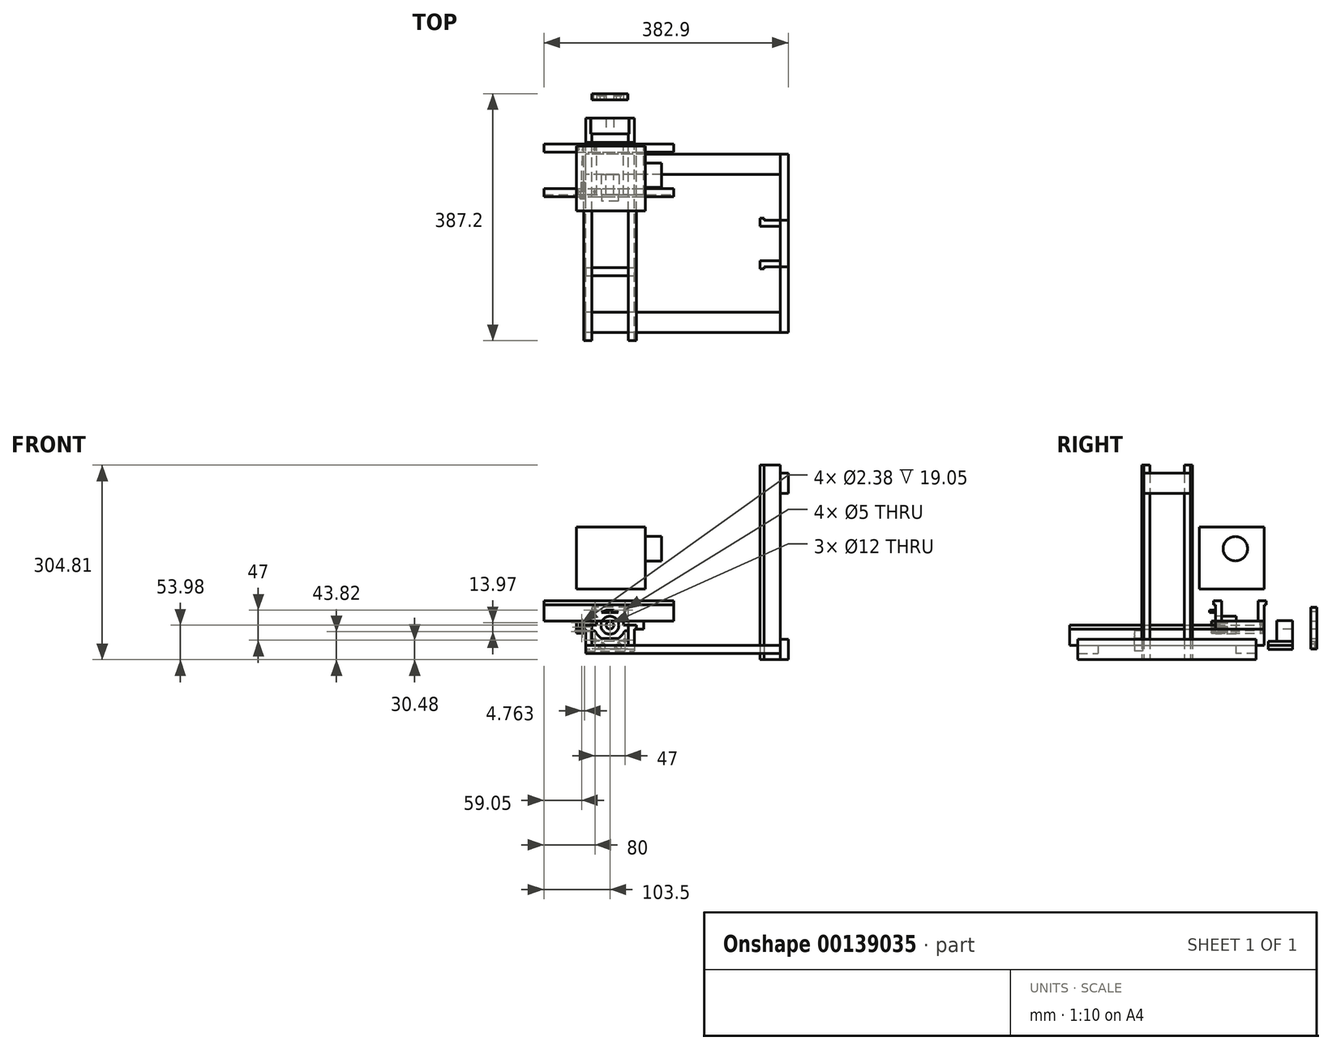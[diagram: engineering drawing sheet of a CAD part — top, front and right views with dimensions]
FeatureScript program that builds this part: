
annotation { "Feature Type Name" : "Feature", "Feature Type Description" : "" }
export const myFeature = defineFeature(function(context is Context, id is Id, definition is map)
    precondition{}
    {
        {
            var Q0;
            Q0=qCreatedBy(makeId("Front.planeOp"),FACE);
            var sketch = newSketch(context, id + "F0", { "sketchPlane" : qUnion([Q0])});
            skLineSegment(sketch, "E0.bottom", {"start": v(-38.1, 0) * mm, "end": v(-28.58, 0) * mm});
            skLineSegment(sketch, "E0.top", {"start": v(-41.27, 31.75) * mm, "end": v(-28.57, 31.75) * mm});
            skLineSegment(sketch, "E0.right", {"start": v(-28.58, 0) * mm, "end": v(-28.57, 31.75) * mm});
            skPoint(sketch, "E1", {"position": v(-41.27, 25.4) * mm});
            skLineSegment(sketch, "E2", {"start": v(-41.27, 31.75) * mm, "end": v(-41.27, 25.4) * mm});
            skLineSegment(sketch, "E3", {"start": v(-38.1, 25.4) * mm, "end": v(-38.1, 0) * mm});
            skLineSegment(sketch, "E4", {"start": v(-41.27, 25.4) * mm, "end": v(-38.1, 25.4) * mm});
            skPoint(sketch, "E5", {"position": v(-33.34, 0) * mm});
            skLineSegment(sketch, "E6.MirrorCS", {"start": v(28.58, 0) * mm, "end": v(28.57, 31.75) * mm});
            skLineSegment(sketch, "E7.MirrorCS", {"start": v(38.1, 0) * mm, "end": v(28.58, 0) * mm});
            skLineSegment(sketch, "E8.MirrorCS", {"start": v(38.1, 25.4) * mm, "end": v(38.1, 0) * mm});
            skLineSegment(sketch, "E9.MirrorCS", {"start": v(41.27, 25.4) * mm, "end": v(38.1, 25.4) * mm});
            skLineSegment(sketch, "E10.MirrorCS", {"start": v(41.27, 31.75) * mm, "end": v(41.27, 25.4) * mm});
            skLineSegment(sketch, "E11.MirrorCS", {"start": v(41.27, 31.75) * mm, "end": v(28.57, 31.75) * mm});
            skSolve(sketch);
        }
        {
            var Q0;
            Q0 = qSketchRegion(id + "F0", true);
            extrude(context, id + "F1", {"entities" : qUnion([Q0]), "depth" : 304.8 * mm});
        }
        {
            var Q0;
            Q0=makeQuery(id+"F1.opExtrude","CAP_FACE",FACE,{"disambiguationData":[OSD([sQuery(id+"F0.wireOp",EDGE,"E0.bottom"),sQuery(id+"F0.wireOp",EDGE,"E0.top"),sQuery(id+"F0.wireOp",EDGE,"E0.right"),sQuery(id+"F0.wireOp",EDGE,"E2"),sQuery(id+"F0.wireOp",EDGE,"E3"),sQuery(id+"F0.wireOp",EDGE,"E4")])],"isStart":true});
            var sketch = newSketch(context, id + "F2", { "sketchPlane" : qUnion([Q0])});
            skLineSegment(sketch, "E12", {"start": v(28.57, 31.75) * mm, "end": v(41.27, 31.75) * mm});
            skLineSegment(sketch, "E13", {"start": v(41.27, 31.75) * mm, "end": v(41.27, 25.4) * mm});
            skLineSegment(sketch, "E14", {"start": v(41.27, 25.4) * mm, "end": v(52.7, 25.4) * mm});
            skLineSegment(sketch, "E15", {"start": v(52.7, 25.4) * mm, "end": v(52.7, 38.1) * mm});
            skLineSegment(sketch, "E16", {"start": v(52.7, 38.1) * mm, "end": v(20.95, 38.1) * mm});
            skLineSegment(sketch, "E17", {"start": v(20.95, 38.1) * mm, "end": v(20.95, 31.75) * mm});
            skLineSegment(sketch, "E18", {"start": v(20.95, 31.75) * mm, "end": v(28.57, 31.75) * mm});
            skLineSegment(sketch, "E19.MirrorCS", {"start": v(-20.95, 38.1) * mm, "end": v(-20.95, 31.75) * mm});
            skLineSegment(sketch, "E20.MirrorCS", {"start": v(-20.95, 31.75) * mm, "end": v(-28.57, 31.75) * mm});
            skLineSegment(sketch, "E21.MirrorCS", {"start": v(-28.57, 31.75) * mm, "end": v(-41.27, 31.75) * mm});
            skLineSegment(sketch, "E22.MirrorCS", {"start": v(-41.27, 31.75) * mm, "end": v(-41.27, 25.4) * mm});
            skLineSegment(sketch, "E23.MirrorCS", {"start": v(-41.27, 25.4) * mm, "end": v(-52.7, 25.4) * mm});
            skLineSegment(sketch, "E24.MirrorCS", {"start": v(-52.7, 25.4) * mm, "end": v(-52.7, 38.1) * mm});
            skLineSegment(sketch, "E25.MirrorCS", {"start": v(-52.7, 38.1) * mm, "end": v(-20.95, 38.1) * mm});
            skSolve(sketch);
        }
        {
            var Q0;
            Q0=makeQuery(id+"F2.imprint","IMPRINT",FACE,{"disambiguationData":[TD([[makeQuery(id+"F2.imprint","IMPRINT",EDGE,{"derivedFrom":sQuery(id+"F2.wireOp",EDGE,"E12")}),-1.0]])]});
            var Q1;
            Q1=makeQuery(id+"F2.imprint","IMPRINT",FACE,{"disambiguationData":[TD([[makeQuery(id+"F2.imprint","IMPRINT",EDGE,{"derivedFrom":sQuery(id+"F2.wireOp",EDGE,"E19.MirrorCS")}),-1.0]])]});
            extrude(context, id + "F3", {"entities" : qUnion([Q0, Q1]), "oppositeDirection" : true, "depth" : 76.2 * mm});
        }
        {
            var Q0;
            Q0=makeQuery(id+"F1.opExtrude","CAP_FACE",FACE,{"disambiguationData":[OSD([sQuery(id+"F0.wireOp",EDGE,"E0.bottom"),sQuery(id+"F0.wireOp",EDGE,"E0.top"),sQuery(id+"F0.wireOp",EDGE,"E0.right"),sQuery(id+"F0.wireOp",EDGE,"E2"),sQuery(id+"F0.wireOp",EDGE,"E3"),sQuery(id+"F0.wireOp",EDGE,"E4")])],"isStart":true});
            var sketch = newSketch(context, id + "F4", { "sketchPlane" : qUnion([Q0])});
            skLineSegment(sketch, "E26.bottom", {"start": v(38.1, 25.4) * mm, "end": v(52.7, 25.4) * mm});
            skLineSegment(sketch, "E26.top", {"start": v(38.1, 19.05) * mm, "end": v(52.7, 19.05) * mm});
            skLineSegment(sketch, "E26.left", {"start": v(38.1, 25.4) * mm, "end": v(38.1, 19.05) * mm});
            skLineSegment(sketch, "E26.right", {"start": v(52.7, 25.4) * mm, "end": v(52.7, 19.05) * mm});
            skSolve(sketch);
        }
        {
            var Q0;
            Q0 = qSketchRegion(id + "F4", true);
            extrude(context, id + "F5", {"entities" : qUnion([Q0]), "oppositeDirection" : true, "depth" : 76.2 * mm});
        }
        {
            var Q0;
            Q0=makeQuery(id+"F3.opExtrude","SWEPT_FACE",FACE,{"disambiguationData":[OSD([sQuery(id+"F2.wireOp",EDGE,"E14")])]});
            var sketch = newSketch(context, id + "F6", { "sketchPlane" : qUnion([Q0])});
            skLineSegment(sketch, "E27", {"start": v(-49.53, 0) * mm, "end": v(-49.53, 76.2) * mm});
            skCircle(sketch, "E28", {"center": v(-49.53, 71.44) * mm, "radius": 1.59 * mm});
            skCircle(sketch, "E29", {"center": v(-49.53, 4.76) * mm, "radius": 1.59 * mm});
            skSolve(sketch);
        }
        {
            var Q0;
            Q0 = qSketchRegion(id + "F6", true);
            extrude(context, id + "F7", {"entities" : qUnion([Q0]), "operationType" : NewBodyOperationType.REMOVE, "oppositeDirection" : true, "depth" : 25.4 * mm, "hasSecondDirection" : true, "secondDirectionOppositeDirection" : false, "secondDirectionDepth" : 25.4 * mm});
        }
        {
            var Q0;
            Q0=makeQuery(id+"F5.opExtrude","SWEPT_FACE",FACE,{"disambiguationData":[OSD([sQuery(id+"F4.wireOp",EDGE,"E26.left")])]});
            var sketch = newSketch(context, id + "F8", { "sketchPlane" : qUnion([Q0])});
            skLineSegment(sketch, "E30", {"start": v(-76.2, 25.4) * mm, "end": v(-76.2, 21.47) * mm});
            skLineSegment(sketch, "E31", {"start": v(-76.2, 21.47) * mm, "end": v(0, 24.13) * mm});
            skLineSegment(sketch, "E32", {"start": v(0, 24.13) * mm, "end": v(0, 25.4) * mm});
            skLineSegment(sketch, "E33", {"start": v(0, 25.4) * mm, "end": v(-76.2, 25.4) * mm});
            skSolve(sketch);
        }
        {
            var Q0;
            Q0=makeQuery(id+"F8.imprint","IMPRINT",FACE,{"disambiguationData":[TD([[makeQuery(id+"F8.imprint","IMPRINT",EDGE,{"derivedFrom":sQuery(id+"F8.wireOp",EDGE,"E30")}),1.0]])]});
            extrude(context, id + "F9", {"entities" : qUnion([Q0]), "operationType" : NewBodyOperationType.REMOVE, "oppositeDirection" : true, "depth" : 3.17 * mm});
        }
        {
            var Q0;
            Q0 = qSketchRegion(id + "F8", true);
            extrude(context, id + "F10", {"entities" : qUnion([Q0]), "oppositeDirection" : true, "depth" : 3.17 * mm});
        }
        {
            var Q0;
            Q0=makeQuery(id+"F3.opExtrude","SWEPT_FACE",FACE,{"disambiguationData":[OSD([sQuery(id+"F2.wireOp",EDGE,"E14")])]});
            var sketch = newSketch(context, id + "F11", { "sketchPlane" : qUnion([Q0])});
            skLineSegment(sketch, "E34", {"start": v(-41.27, 76.2) * mm, "end": v(-45.2, 76.2) * mm});
            skLineSegment(sketch, "E35", {"start": v(-45.2, 76.2) * mm, "end": v(-42.54, 0) * mm});
            skLineSegment(sketch, "E36", {"start": v(-42.54, 0) * mm, "end": v(-41.27, 0) * mm});
            skLineSegment(sketch, "E37", {"start": v(-41.27, 0) * mm, "end": v(-41.27, 76.2) * mm});
            skSolve(sketch);
        }
        {
            var Q0;
            Q0=makeQuery(id+"F11.imprint","IMPRINT",FACE,{"disambiguationData":[TD([[makeQuery(id+"F11.imprint","IMPRINT",EDGE,{"derivedFrom":sQuery(id+"F11.wireOp",EDGE,"E34")}),1.0]])]});
            extrude(context, id + "F12", {"entities" : qUnion([Q0]), "operationType" : NewBodyOperationType.REMOVE, "oppositeDirection" : true, "depth" : 6.35 * mm});
        }
        {
            var Q0;
            Q0 = qSketchRegion(id + "F11", true);
            extrude(context, id + "F13", {"entities" : qUnion([Q0]), "oppositeDirection" : true, "depth" : 6.35 * mm});
        }
        {
            var Q0;
            Q0=makeQuery(id+"F3.opExtrude","CAP_FACE",FACE,{"disambiguationData":[OSD([sQuery(id+"F2.wireOp",EDGE,"E12"),sQuery(id+"F2.wireOp",EDGE,"E13"),sQuery(id+"F2.wireOp",EDGE,"E14"),sQuery(id+"F2.wireOp",EDGE,"E15"),sQuery(id+"F2.wireOp",EDGE,"E16"),sQuery(id+"F2.wireOp",EDGE,"E17"),sQuery(id+"F2.wireOp",EDGE,"E18")])],"isStart":false});
            var sketch = newSketch(context, id + "F14", { "sketchPlane" : qUnion([Q0])});
            skLineSegment(sketch, "E38", {"start": v(-41.27, 38.1) * mm, "end": v(-41.27, 25.4) * mm});
            skLineSegment(sketch, "E39", {"start": v(-41.27, 25.4) * mm, "end": v(-38.1, 25.4) * mm});
            skLineSegment(sketch, "E40", {"start": v(-38.1, 25.4) * mm, "end": v(-38.1, 19.05) * mm});
            skLineSegment(sketch, "E41", {"start": v(-38.1, 19.05) * mm, "end": v(-46.99, 19.05) * mm});
            skLineSegment(sketch, "E42", {"start": v(-46.99, 19.05) * mm, "end": v(-46.99, 38.1) * mm});
            skLineSegment(sketch, "E43", {"start": v(-46.99, 38.1) * mm, "end": v(-41.27, 38.1) * mm});
            skSolve(sketch);
        }
        {
            var Q0;
            {var subQ3=sQuery(id+"F14.wireOp",EDGE,"E43");Q0=makeQuery(id+"F14.imprint","IMPRINT",FACE,{"disambiguationData":[TD([[makeQuery(id+"F14.imprint","IMPRINT",EDGE,{"derivedFrom":subQ3}),-1.0]])]});}
            var Q1;
            {var subQ7=sQuery(id+"F14.wireOp",EDGE,"E39");Q1=makeQuery(id+"F14.imprint","IMPRINT",FACE,{"disambiguationData":[TD([[makeQuery(id+"F14.imprint","IMPRINT",EDGE,{"derivedFrom":subQ7}),-1.0]])]});}
            extrude(context, id + "F15", {"entities" : qUnion([Q0, Q1]), "depth" : 6.35 * mm});
        }
        {
            var Q0;
            Q0=makeQuery(id+"F15.opExtrude","CAP_FACE",FACE,{"disambiguationData":[OSD([sQuery(id+"F14.wireOp",EDGE,"E38"),sQuery(id+"F14.wireOp",EDGE,"E39"),sQuery(id+"F14.wireOp",EDGE,"E40"),sQuery(id+"F14.wireOp",EDGE,"E41"),sQuery(id+"F14.wireOp",EDGE,"E42"),sQuery(id+"F14.wireOp",EDGE,"E43")])],"isStart":false});
            var sketch = newSketch(context, id + "F16", { "sketchPlane" : qUnion([Q0])});
            skCircle(sketch, "E44", {"center": v(-44.45, 35.56) * mm, "radius": 1.2 * mm});
            skCircle(sketch, "E45", {"center": v(-44.45, 21.6) * mm, "radius": 1.2 * mm});
            skCircle(sketch, "E46", {"center": v(-42.86, 28.58) * mm, "radius": 1.2 * mm});
            skCircle(sketch, "E47", {"center": v(-39.69, 23.81) * mm, "radius": 1.2 * mm});
            skLineSegment(sketch, "E48", {"start": v(-41.27, 31.75) * mm, "end": v(-41.27, 25.4) * mm});
            skLineSegment(sketch, "E49", {"start": v(-41.27, 28.58) * mm, "end": v(-46.36, 28.58) * mm});
            skLineSegment(sketch, "E50", {"start": v(-39.69, 25.4) * mm, "end": v(-39.69, 13.74) * mm});
            skSolve(sketch);
        }
        {
            var Q0;
            Q0=makeQuery(id+"F16.imprint","IMPRINT",FACE,{"disambiguationData":[TD([[makeQuery(id+"F16.imprint","IMPRINT",EDGE,{"derivedFrom":sQuery(id+"F16.wireOp",EDGE,"E44")}),1.0]])]});
            var Q1;
            Q1=makeQuery(id+"F16.imprint","IMPRINT",FACE,{"disambiguationData":[TD([[makeQuery(id+"F16.imprint","IMPRINT",EDGE,{"derivedFrom":sQuery(id+"F16.wireOp",EDGE,"E45")}),1.0]])]});
            extrude(context, id + "F17", {"entities" : qUnion([Q0, Q1]), "operationType" : NewBodyOperationType.REMOVE, "oppositeDirection" : true, "depth" : 25.4 * mm});
        }
        {
            var Q0;
            Q0 = qSketchRegion(id + "F16", true);
            extrude(context, id + "F18", {"entities" : qUnion([Q0]), "operationType" : NewBodyOperationType.REMOVE, "oppositeDirection" : true, "depth" : 25.4 * mm});
        }
        {
            var Q0;
            Q0=makeQuery(id+"F3.opExtrude","SWEPT_FACE",FACE,{"disambiguationData":[OSD([sQuery(id+"F2.wireOp",EDGE,"E16")])]});
            var sketch = newSketch(context, id + "F19", { "sketchPlane" : qUnion([Q0])});
            skLineSegment(sketch, "E51", {"start": v(-49.53, -4.76) * mm, "end": v(-20.95, -4.76) * mm});
            skLineSegment(sketch, "E52", {"start": v(-49.53, -71.44) * mm, "end": v(-20.95, -71.44) * mm});
            skCircle(sketch, "E53", {"center": v(-24.13, -4.76) * mm, "radius": 1.59 * mm});
            skLineSegment(sketch, "E54", {"start": v(-24.13, -4.76) * mm, "end": v(-24.13, -71.44) * mm});
            skCircle(sketch, "E55", {"center": v(-24.13, -71.44) * mm, "radius": 1.59 * mm});
            skSolve(sketch);
        }
        {
            var Q0;
            Q0 = qSketchRegion(id + "F19", true);
            extrude(context, id + "F20", {"entities" : qUnion([Q0]), "operationType" : NewBodyOperationType.REMOVE, "oppositeDirection" : true, "depth" : 25.4 * mm});
        }
        {
            var Q0;
            Q0=qCreatedBy(makeId("Front.planeOp"),FACE);
            cPlane(context, id + "F21", {"entities" : qUnion([Q0]), "cplaneType" : CPlaneType.OFFSET, "offset" : 76.2 * mm + 10 * mm, "width" : 152.4 * mm, "height" : 152.4 * mm});
        }
        {
            var Q0;
            Q0=qCreatedBy(id+"F21.planeOp",FACE);
            var sketch = newSketch(context, id + "F22", { "sketchPlane" : qUnion([Q0])});
            skCircle(sketch, "E56", {"center": v(0, 31.75) * mm, "radius": 24 * mm});
            skLineSegment(sketch, "E57.bottom", {"start": v(25, 11.75) * mm, "end": v(-25, 11.75) * mm});
            skLineSegment(sketch, "E57.top", {"start": v(25, 51.75) * mm, "end": v(-25, 51.75) * mm});
            skLineSegment(sketch, "E57.left", {"start": v(25, 11.75) * mm, "end": v(25, 51.75) * mm});
            skLineSegment(sketch, "E57.right", {"start": v(-25, 11.75) * mm, "end": v(-25, 51.75) * mm});
            skPoint(sketch, "E58", {"position": v(25, 31.75) * mm});
            skPoint(sketch, "E59", {"position": v(0, 51.75) * mm});
            skSolve(sketch);
        }
        {
            var Q0;
            {var subQ0=sQuery(id+"F22.wireOp",EDGE,"E57.top");var subQ1=sQuery(id+"F22.wireOp",EDGE,"E56");var subQ2=makeQuery(id+"F22.imprint","INTERSECT",VERTEX,{"disambiguationData":[OD(0.0)],"derivedFrom":[subQ1,subQ0]});Q0=makeQuery(id+"F22.imprint","IMPRINT",FACE,{"disambiguationData":[TD([[makeQuery(id+"F22.imprint","IMPRINT",EDGE,{"disambiguationData":[TD([[subQ2,-1.0]])],"derivedFrom":subQ1}),1.0]])]});}
            extrude(context, id + "F23", {"entities" : qUnion([Q0]), "oppositeDirection" : true, "depth" : 10 * mm});
        }
        {
            var Q0;
            Q0=makeQuery(id+"F23.opExtrude","CAP_FACE",FACE,{"disambiguationData":[OSD([sQuery(id+"F22.wireOp",EDGE,"E56"),sQuery(id+"F22.wireOp",EDGE,"E57.bottom"),sQuery(id+"F22.wireOp",EDGE,"E57.top")])],"isStart":false});
            var sketch = newSketch(context, id + "F24", { "sketchPlane" : qUnion([Q0])});
            skLineSegment(sketch, "E60", {"start": v(0, 51.75) * mm, "end": v(0, 11.75) * mm});
            skCircle(sketch, "E61", {"center": v(0, 31.75) * mm, "radius": 14 * mm});
            skLineSegment(sketch, "E62", {"start": v(13.27, 11.75) * mm, "end": v(-13.27, 11.75) * mm});
            skPoint(sketch, "E63", {"position": v(0, 11.75) * mm});
            skSolve(sketch);
        }
        {
            var Q0;
            Q0 = qSketchRegion(id + "F24", true);
            extrude(context, id + "F25", {"entities" : qUnion([Q0]), "operationType" : NewBodyOperationType.ADD, "depth" : 32 * mm});
        }
        {
            var Q0;
            Q0=makeQuery(id+"F23.opExtrude","CAP_FACE",FACE,{"disambiguationData":[OSD([sQuery(id+"F22.wireOp",EDGE,"E56"),sQuery(id+"F22.wireOp",EDGE,"E57.bottom"),sQuery(id+"F22.wireOp",EDGE,"E57.top")])],"isStart":false});
            var sketch = newSketch(context, id + "F26", { "sketchPlane" : qUnion([Q0])});
            skLineSegment(sketch, "E64", {"start": v(-13.27, 51.75) * mm, "end": v(13.27, 11.75) * mm});
            skLineSegment(sketch, "E65", {"start": v(0, 31.75) * mm, "end": v(-18.94, 31.75) * mm});
            skPoint(sketch, "E65.endSnap0", {"position": v(-24, 31.75) * mm});
            skCircle(sketch, "E66", {"center": v(0, 31.75) * mm, "radius": 19 * mm});
            skCircle(sketch, "E67", {"center": v(-18.94, 31.75) * mm, "radius": 2.75 * mm});
            skCircle(sketch, "E68.1.0", {"center": v(-13.4, 18.36) * mm, "radius": 2.75 * mm});
            skCircle(sketch, "E68.2.0", {"center": v(0, 12.81) * mm, "radius": 2.75 * mm});
            skCircle(sketch, "E68.3.0", {"center": v(13.4, 18.36) * mm, "radius": 2.75 * mm});
            skCircle(sketch, "E68.4.0", {"center": v(18.94, 31.75) * mm, "radius": 2.75 * mm});
            skCircle(sketch, "E68.5.0", {"center": v(13.4, 45.14) * mm, "radius": 2.75 * mm});
            skCircle(sketch, "E68.6.0", {"center": v(0, 50.69) * mm, "radius": 2.75 * mm});
            skCircle(sketch, "E68.7.0", {"center": v(-13.4, 45.14) * mm, "radius": 2.75 * mm});
            skSolve(sketch);
        }
        {
            var Q0;
            {var subQ0=sQuery(id+"F26.wireOp",EDGE,"E68.7.0");var subQ1=sQuery(id+"F26.wireOp",EDGE,"E66");var subQ2=makeQuery(id+"F26.imprint","INTERSECT",VERTEX,{"disambiguationData":[OD(0.0)],"derivedFrom":[subQ1,subQ0]});Q0=makeQuery(id+"F26.imprint","IMPRINT",FACE,{"disambiguationData":[TD([[makeQuery(id+"F26.imprint","IMPRINT",EDGE,{"disambiguationData":[TD([[subQ2,-1.0]])],"derivedFrom":subQ1}),1.0]])]});}
            var Q1;
            {var subQ0=sQuery(id+"F26.wireOp",EDGE,"E68.7.0");var subQ1=sQuery(id+"F26.wireOp",EDGE,"E66");var subQ2=makeQuery(id+"F26.imprint","INTERSECT",VERTEX,{"disambiguationData":[OD(0.0)],"derivedFrom":[subQ1,subQ0]});Q1=makeQuery(id+"F26.imprint","IMPRINT",FACE,{"disambiguationData":[TD([[makeQuery(id+"F26.imprint","IMPRINT",EDGE,{"disambiguationData":[TD([[subQ2,-1.0]])],"derivedFrom":subQ1}),-1.0]])]});}
            var Q2;
            {var subQ0=sQuery(id+"F26.wireOp",EDGE,"E67");var subQ1=sQuery(id+"F26.wireOp",EDGE,"E66");var subQ2=makeQuery(id+"F26.imprint","INTERSECT",VERTEX,{"disambiguationData":[OD(0.0)],"derivedFrom":[subQ1,subQ0]});Q2=makeQuery(id+"F26.imprint","IMPRINT",FACE,{"disambiguationData":[TD([[makeQuery(id+"F26.imprint","IMPRINT",EDGE,{"disambiguationData":[TD([[subQ2,-1.0]])],"derivedFrom":subQ1}),-1.0]])]});}
            var Q3;
            {var subQ0=sQuery(id+"F26.wireOp",EDGE,"E67");var subQ1=sQuery(id+"F26.wireOp",EDGE,"E66");var subQ2=makeQuery(id+"F26.imprint","INTERSECT",VERTEX,{"disambiguationData":[OD(0.0)],"derivedFrom":[subQ1,subQ0]});Q3=makeQuery(id+"F26.imprint","IMPRINT",FACE,{"disambiguationData":[TD([[makeQuery(id+"F26.imprint","IMPRINT",EDGE,{"disambiguationData":[TD([[subQ2,-1.0]])],"derivedFrom":subQ1}),1.0]])]});}
            var Q4;
            {var subQ0=sQuery(id+"F26.wireOp",EDGE,"E68.1.0");var subQ1=sQuery(id+"F26.wireOp",EDGE,"E66");var subQ2=makeQuery(id+"F26.imprint","INTERSECT",VERTEX,{"disambiguationData":[OD(0.0)],"derivedFrom":[subQ1,subQ0]});Q4=makeQuery(id+"F26.imprint","IMPRINT",FACE,{"disambiguationData":[TD([[makeQuery(id+"F26.imprint","IMPRINT",EDGE,{"disambiguationData":[TD([[subQ2,-1.0]])],"derivedFrom":subQ1}),-1.0]])]});}
            var Q5;
            {var subQ0=sQuery(id+"F26.wireOp",EDGE,"E68.1.0");var subQ1=sQuery(id+"F26.wireOp",EDGE,"E66");var subQ2=makeQuery(id+"F26.imprint","INTERSECT",VERTEX,{"disambiguationData":[OD(0.0)],"derivedFrom":[subQ1,subQ0]});Q5=makeQuery(id+"F26.imprint","IMPRINT",FACE,{"disambiguationData":[TD([[makeQuery(id+"F26.imprint","IMPRINT",EDGE,{"disambiguationData":[TD([[subQ2,-1.0]])],"derivedFrom":subQ1}),1.0]])]});}
            var Q6;
            {var subQ0=sQuery(id+"F26.wireOp",EDGE,"E68.3.0");var subQ1=sQuery(id+"F26.wireOp",EDGE,"E66");var subQ2=makeQuery(id+"F26.imprint","INTERSECT",VERTEX,{"disambiguationData":[OD(0.0)],"derivedFrom":[subQ1,subQ0]});Q6=makeQuery(id+"F26.imprint","IMPRINT",FACE,{"disambiguationData":[TD([[makeQuery(id+"F26.imprint","IMPRINT",EDGE,{"disambiguationData":[TD([[subQ2,-1.0]])],"derivedFrom":subQ1}),-1.0]])]});}
            var Q7;
            {var subQ0=sQuery(id+"F26.wireOp",EDGE,"E68.3.0");var subQ1=sQuery(id+"F26.wireOp",EDGE,"E66");var subQ2=makeQuery(id+"F26.imprint","INTERSECT",VERTEX,{"disambiguationData":[OD(0.0)],"derivedFrom":[subQ1,subQ0]});Q7=makeQuery(id+"F26.imprint","IMPRINT",FACE,{"disambiguationData":[TD([[makeQuery(id+"F26.imprint","IMPRINT",EDGE,{"disambiguationData":[TD([[subQ2,-1.0]])],"derivedFrom":subQ1}),1.0]])]});}
            var Q8;
            {var subQ0=sQuery(id+"F26.wireOp",EDGE,"E68.4.0");var subQ1=sQuery(id+"F26.wireOp",EDGE,"E66");var subQ2=makeQuery(id+"F26.imprint","INTERSECT",VERTEX,{"disambiguationData":[OD(0.0)],"derivedFrom":[subQ1,subQ0]});Q8=makeQuery(id+"F26.imprint","IMPRINT",FACE,{"disambiguationData":[TD([[makeQuery(id+"F26.imprint","IMPRINT",EDGE,{"disambiguationData":[TD([[subQ2,1.0]])],"derivedFrom":subQ1}),1.0]])]});}
            var Q9;
            {var subQ0=sQuery(id+"F26.wireOp",EDGE,"E68.4.0");var subQ1=sQuery(id+"F26.wireOp",EDGE,"E66");var subQ2=makeQuery(id+"F26.imprint","INTERSECT",VERTEX,{"disambiguationData":[OD(0.0)],"derivedFrom":[subQ1,subQ0]});Q9=makeQuery(id+"F26.imprint","IMPRINT",FACE,{"disambiguationData":[TD([[makeQuery(id+"F26.imprint","IMPRINT",EDGE,{"disambiguationData":[TD([[subQ2,1.0]])],"derivedFrom":subQ1}),-1.0]])]});}
            var Q10;
            {var subQ0=sQuery(id+"F26.wireOp",EDGE,"E68.5.0");var subQ1=sQuery(id+"F26.wireOp",EDGE,"E66");var subQ2=makeQuery(id+"F26.imprint","INTERSECT",VERTEX,{"disambiguationData":[OD(0.0)],"derivedFrom":[subQ1,subQ0]});Q10=makeQuery(id+"F26.imprint","IMPRINT",FACE,{"disambiguationData":[TD([[makeQuery(id+"F26.imprint","IMPRINT",EDGE,{"disambiguationData":[TD([[subQ2,-1.0]])],"derivedFrom":subQ1}),-1.0]])]});}
            var Q11;
            {var subQ0=sQuery(id+"F26.wireOp",EDGE,"E68.5.0");var subQ1=sQuery(id+"F26.wireOp",EDGE,"E66");var subQ2=makeQuery(id+"F26.imprint","INTERSECT",VERTEX,{"disambiguationData":[OD(0.0)],"derivedFrom":[subQ1,subQ0]});Q11=makeQuery(id+"F26.imprint","IMPRINT",FACE,{"disambiguationData":[TD([[makeQuery(id+"F26.imprint","IMPRINT",EDGE,{"disambiguationData":[TD([[subQ2,-1.0]])],"derivedFrom":subQ1}),1.0]])]});}
            extrude(context, id + "F27", {"entities" : qUnion([Q0, Q1, Q2, Q3, Q4, Q5, Q6, Q7, Q8, Q9, Q10, Q11]), "operationType" : NewBodyOperationType.REMOVE, "oppositeDirection" : true, "depth" : 25.4 * mm});
        }
        {
            var Q0;
            Q0=makeQuery(id+"F25.opExtrude","CAP_FACE",FACE,{"disambiguationData":[OSD([sQuery(id+"F24.wireOp",EDGE,"E61")])],"isStart":false});
            var sketch = newSketch(context, id + "F28", { "sketchPlane" : qUnion([Q0])});
            skPoint(sketch, "E69", {"position": v(0, 31.75) * mm});
            skLineSegment(sketch, "E70.bottom", {"start": v(-30, 6.75) * mm, "end": v(30, 6.75) * mm});
            skLineSegment(sketch, "E70.top", {"start": v(-30, 39.25) * mm, "end": v(30, 39.25) * mm});
            skLineSegment(sketch, "E70.left", {"start": v(-30, 6.75) * mm, "end": v(-30, 39.25) * mm});
            skLineSegment(sketch, "E70.right", {"start": v(30, 6.75) * mm, "end": v(30, 39.25) * mm});
            skPoint(sketch, "E71", {"position": v(0, 39.25) * mm});
            skPoint(sketch, "E72", {"position": v(-30, 31.75) * mm});
            skCircle(sketch, "E73", {"center": v(0, 31.75) * mm, "radius": 6 * mm});
            skSolve(sketch);
        }
        {
            var Q0;
            Q0=makeQuery(id+"F28.imprint","IMPRINT",FACE,{"disambiguationData":[TD([[makeQuery(id+"F28.imprint","IMPRINT",EDGE,{"derivedFrom":sQuery(id+"F28.wireOp",EDGE,"E70.bottom")}),1.0]])]});
            var Q1;
            Q1=makeQuery(id+"F28.imprint","IMPRINT",FACE,{"disambiguationData":[TD([[makeQuery(id+"F28.imprint","IMPRINT",EDGE,{"derivedFrom":sQuery(id+"F28.wireOp",EDGE,"E73")}),-1.0]])]});
            extrude(context, id + "F29", {"entities" : qUnion([Q0, Q1]), "depth" : 63.5 * mm + 25 * mm, "hasSecondDirection" : true, "secondDirectionOppositeDirection" : false, "secondDirectionDepth" : 63.5 * mm});
        }
        {
            var Q0;
            Q0=makeQuery(id+"F28.imprint","IMPRINT",FACE,{"disambiguationData":[TD([[makeQuery(id+"F28.imprint","IMPRINT",EDGE,{"derivedFrom":sQuery(id+"F28.wireOp",EDGE,"E73")}),1.0]])]});
            extrude(context, id + "F30", {"entities" : qUnion([Q0]), "operationType" : NewBodyOperationType.REMOVE, "oppositeDirection" : true, "depth" : 50.8 * mm});
        }
        {
            var Q0;
            Q0=makeQuery(id+"F23.opExtrude","SWEPT_FACE",FACE,{"disambiguationData":[OSD([sQuery(id+"F22.wireOp",EDGE,"E57.top")])]});
            var sketch = newSketch(context, id + "F31", { "sketchPlane" : qUnion([Q0])});
            skLineSegment(sketch, "E74.bottom", {"start": v(-16.65, -76.2) * mm, "end": v(15.58, -76.2) * mm});
            skLineSegment(sketch, "E74.top", {"start": v(-16.65, -42.02) * mm, "end": v(15.58, -42.02) * mm});
            skLineSegment(sketch, "E74.left", {"start": v(-16.65, -76.2) * mm, "end": v(-16.65, -42.02) * mm});
            skLineSegment(sketch, "E74.right", {"start": v(15.58, -76.2) * mm, "end": v(15.58, -42.02) * mm});
            skSolve(sketch);
        }
        {
            var Q0;
            Q0 = qSketchRegion(id + "F31", true);
            extrude(context, id + "F32", {"entities" : qUnion([Q0]), "operationType" : NewBodyOperationType.REMOVE, "oppositeDirection" : true, "depth" : 101.6 * mm});
        }
        {
            var Q0;
            Q0=makeQuery(id+"F3.opExtrude","SWEPT_FACE",FACE,{"disambiguationData":[OSD([sQuery(id+"F2.wireOp",EDGE,"E15")])]});
            var sketch = newSketch(context, id + "F33", { "sketchPlane" : qUnion([Q0])});
            skLineSegment(sketch, "E75", {"start": v(66.68, 69.85) * mm, "end": v(66.68, 38.1) * mm});
            skLineSegment(sketch, "E76", {"start": v(66.68, 38.1) * mm, "end": v(76.2, 38.1) * mm});
            skLineSegment(sketch, "E77", {"start": v(76.2, 38.1) * mm, "end": v(76.2, 63.5) * mm});
            skLineSegment(sketch, "E78", {"start": v(76.2, 63.5) * mm, "end": v(79.38, 63.5) * mm});
            skLineSegment(sketch, "E79", {"start": v(79.38, 63.5) * mm, "end": v(79.38, 69.85) * mm});
            skLineSegment(sketch, "E80", {"start": v(79.38, 69.85) * mm, "end": v(66.68, 69.85) * mm});
            skPoint(sketch, "E81", {"position": v(71.44, 38.1) * mm});
            skPoint(sketch, "E82", {"position": v(38.1, 38.1) * mm});
            skLineSegment(sketch, "E83", {"start": v(38.1, 38.1) * mm, "end": v(38.1, 64.34) * mm});
            skLineSegment(sketch, "E84.MirrorCS", {"start": v(9.53, 69.85) * mm, "end": v(9.53, 38.1) * mm});
            skLineSegment(sketch, "E85.MirrorCS", {"start": v(9.53, 38.1) * mm, "end": v(0, 38.1) * mm});
            skLineSegment(sketch, "E86.MirrorCS", {"start": v(0, 38.1) * mm, "end": v(0, 63.5) * mm});
            skLineSegment(sketch, "E87.MirrorCS", {"start": v(0, 63.5) * mm, "end": v(-3.17, 63.5) * mm});
            skLineSegment(sketch, "E88.MirrorCS", {"start": v(-3.17, 63.5) * mm, "end": v(-3.17, 69.85) * mm});
            skLineSegment(sketch, "E89.MirrorCS", {"start": v(-3.17, 69.85) * mm, "end": v(9.53, 69.85) * mm});
            skSolve(sketch);
        }
        {
            var Q0;
            Q0 = qSketchRegion(id + "F33", true);
            extrude(context, id + "F34", {"entities" : qUnion([Q0]), "depth" : 50.8 * mm, "hasSecondDirection" : true, "secondDirectionOppositeDirection" : true, "secondDirectionDepth" : 152.4 * mm});
        }
        {
            var Q0;
            Q0=makeQuery(id+"F1.opExtrude","CAP_FACE",FACE,{"disambiguationData":[OSD([sQuery(id+"F0.wireOp",EDGE,"E0.bottom"),sQuery(id+"F0.wireOp",EDGE,"E0.top"),sQuery(id+"F0.wireOp",EDGE,"E0.right"),sQuery(id+"F0.wireOp",EDGE,"E2"),sQuery(id+"F0.wireOp",EDGE,"E3"),sQuery(id+"F0.wireOp",EDGE,"E4")])],"isStart":false});
            var sketch = newSketch(context, id + "F35", { "sketchPlane" : qUnion([Q0])});
            skLineSegment(sketch, "E90", {"start": v(-28.58, 0) * mm, "end": v(-28.57, 23.07) * mm});
            skLineSegment(sketch, "E91", {"start": v(-28.57, 23.07) * mm, "end": v(-24.73, 23.07) * mm});
            skLineSegment(sketch, "E92", {"start": v(-22.42, 21.6) * mm, "end": v(-21.22, 19) * mm});
            skLineSegment(sketch, "E93", {"start": v(-19.91, 17.13) * mm, "end": v(-15.37, 12.66) * mm});
            skLineSegment(sketch, "E94", {"start": v(-10.91, 10.84) * mm, "end": v(0, 10.84) * mm});
            skLineSegment(sketch, "E95", {"start": v(0, 10.84) * mm, "end": v(0, 0) * mm});
            skLineSegment(sketch, "E96", {"start": v(0, 0) * mm, "end": v(-28.58, 0) * mm});
            skPoint(sketch, "E97.visualSharp", {"position": v(-20.73, 17.94) * mm});
            skArc(sketch, "E97.filletArc", {"start": v(-21.22, 19) * mm, "mid": v(-20.65, 18) * mm, "end": v(-19.91, 17.13) * mm});
            skPoint(sketch, "E98.visualSharp", {"position": v(-13.51, 10.84) * mm});
            skArc(sketch, "E98.filletArc", {"start": v(-15.37, 12.66) * mm, "mid": v(-13.32, 11.3) * mm, "end": v(-10.91, 10.84) * mm});
            skPoint(sketch, "E99.visualSharp", {"position": v(-23.1, 23.07) * mm});
            skArc(sketch, "E99.filletArc", {"start": v(-22.42, 21.6) * mm, "mid": v(-23.36, 22.67) * mm, "end": v(-24.73, 23.07) * mm});
            skLineSegment(sketch, "E100.MirrorCS", {"start": v(10.91, 10.84) * mm, "end": v(0, 10.84) * mm});
            skArc(sketch, "E101.MirrorCS", {"start": v(15.37, 12.66) * mm, "mid": v(13.32, 11.3) * mm, "end": v(10.91, 10.84) * mm});
            skLineSegment(sketch, "E102.MirrorCS", {"start": v(19.91, 17.13) * mm, "end": v(15.37, 12.66) * mm});
            skArc(sketch, "E103.MirrorCS", {"start": v(21.22, 19) * mm, "mid": v(20.65, 18) * mm, "end": v(19.91, 17.13) * mm});
            skLineSegment(sketch, "E104.MirrorCS", {"start": v(22.42, 21.6) * mm, "end": v(21.22, 19) * mm});
            skArc(sketch, "E105.MirrorCS", {"start": v(22.42, 21.6) * mm, "mid": v(23.36, 22.67) * mm, "end": v(24.73, 23.07) * mm});
            skLineSegment(sketch, "E106.MirrorCS", {"start": v(28.57, 23.07) * mm, "end": v(24.73, 23.07) * mm});
            skLineSegment(sketch, "E107.MirrorCS", {"start": v(28.58, 0) * mm, "end": v(28.58, 23.07) * mm});
            skLineSegment(sketch, "E108.MirrorCS", {"start": v(0, 0) * mm, "end": v(28.58, 0) * mm});
            skLineSegment(sketch, "E109", {"start": v(-28.58, 0) * mm, "end": v(-38.1, 0) * mm});
            skLineSegment(sketch, "E110", {"start": v(-38.1, 0) * mm, "end": v(-38.1, -8.68) * mm});
            skLineSegment(sketch, "E111", {"start": v(-38.1, -8.68) * mm, "end": v(0, -8.68) * mm});
            skLineSegment(sketch, "E112", {"start": v(0, -8.68) * mm, "end": v(0, 0) * mm});
            skLineSegment(sketch, "E113.MirrorCS", {"start": v(28.58, 0) * mm, "end": v(38.1, 0) * mm});
            skLineSegment(sketch, "E114.MirrorCS", {"start": v(38.1, 0) * mm, "end": v(38.1, -8.68) * mm});
            skLineSegment(sketch, "E115.MirrorCS", {"start": v(38.1, -8.68) * mm, "end": v(0, -8.68) * mm});
            skSolve(sketch);
        }
        {
            var Q0;
            Q0=makeQuery(id+"F35.imprint","IMPRINT",FACE,{"disambiguationData":[TD([[makeQuery(id+"F35.imprint","IMPRINT",EDGE,{"derivedFrom":sQuery(id+"F35.wireOp",EDGE,"E90")}),-1.0]])]});
            var Q1;
            Q1=makeQuery(id+"F35.imprint","IMPRINT",FACE,{"disambiguationData":[TD([[makeQuery(id+"F35.imprint","IMPRINT",EDGE,{"derivedFrom":sQuery(id+"F35.wireOp",EDGE,"E95")}),1.0]])]});
            var Q2;
            Q2=makeQuery(id+"F35.imprint","IMPRINT",FACE,{"disambiguationData":[TD([[makeQuery(id+"F35.imprint","IMPRINT",EDGE,{"derivedFrom":sQuery(id+"F35.wireOp",EDGE,"E96")}),1.0]])]});
            var Q3;
            Q3=makeQuery(id+"F35.imprint","IMPRINT",FACE,{"disambiguationData":[TD([[makeQuery(id+"F35.imprint","IMPRINT",EDGE,{"derivedFrom":sQuery(id+"F35.wireOp",EDGE,"E108.MirrorCS")}),-1.0]])]});
            extrude(context, id + "F36", {"entities" : qUnion([Q0, Q1, Q2, Q3]), "oppositeDirection" : true, "depth" : 114.3 * mm, "hasSecondDirection" : true, "secondDirectionOppositeDirection" : true, "secondDirectionDepth" : 101.6 * mm});
        }
        {
            var Q0;
            Q0=makeQuery(id+"F29.opExtrude","CAP_FACE",FACE,{"disambiguationData":[OSD([sQuery(id+"F28.wireOp",EDGE,"E70.bottom"),sQuery(id+"F28.wireOp",EDGE,"E70.top"),sQuery(id+"F28.wireOp",EDGE,"E70.left"),sQuery(id+"F28.wireOp",EDGE,"E70.right"),sQuery(id+"F28.wireOp",EDGE,"E73")])],"isStart":false});
            var sketch = newSketch(context, id + "F37", { "sketchPlane" : qUnion([Q0])});
            skLineSegment(sketch, "E116.bottom", {"start": v(-28.58, 6.75) * mm, "end": v(28.58, 6.75) * mm});
            skLineSegment(sketch, "E116.top", {"start": v(-28.58, -5.95) * mm, "end": v(28.58, -5.95) * mm});
            skLineSegment(sketch, "E116.left", {"start": v(-28.58, 6.75) * mm, "end": v(-28.58, -5.95) * mm});
            skLineSegment(sketch, "E116.right", {"start": v(28.58, 6.75) * mm, "end": v(28.58, -5.95) * mm});
            skPoint(sketch, "E117", {"position": v(0, -5.95) * mm});
            skLineSegment(sketch, "E118", {"start": v(28.58, 0) * mm, "end": v(38.1, 0) * mm});
            skLineSegment(sketch, "E119", {"start": v(38.1, 0) * mm, "end": v(38.1, -5.95) * mm});
            skLineSegment(sketch, "E120", {"start": v(38.1, -5.95) * mm, "end": v(28.58, -5.95) * mm});
            skLineSegment(sketch, "E121", {"start": v(0, -5.95) * mm, "end": v(0, 6.75) * mm});
            skLineSegment(sketch, "E122.MirrorCS", {"start": v(-38.1, -5.95) * mm, "end": v(-28.58, -5.95) * mm});
            skLineSegment(sketch, "E123.MirrorCS", {"start": v(-38.1, 0) * mm, "end": v(-38.1, -5.95) * mm});
            skLineSegment(sketch, "E124.MirrorCS", {"start": v(-28.58, 0) * mm, "end": v(-38.1, 0) * mm});
            skSolve(sketch);
        }
        {
            var Q0;
            Q0 = qSketchRegion(id + "F37", true);
            extrude(context, id + "F38", {"entities" : qUnion([Q0]), "oppositeDirection" : true, "depth" : 38.1 * mm});
        }
        {
            var Q0;
            Q0=makeQuery(id+"F1.opExtrude","SWEPT_FACE",FACE,{"disambiguationData":[OSD([sQuery(id+"F0.wireOp",EDGE,"E3")])]});
            var sketch = newSketch(context, id + "F39", { "sketchPlane" : qUnion([Q0])});
            skLineSegment(sketch, "E125.bottom", {"start": v(12.7, 0) * mm, "end": v(44.45, 0) * mm});
            skLineSegment(sketch, "E125.top", {"start": v(12.7, -12.7) * mm, "end": v(44.45, -12.7) * mm});
            skLineSegment(sketch, "E125.left", {"start": v(12.7, 0) * mm, "end": v(12.7, -12.7) * mm});
            skLineSegment(sketch, "E125.right", {"start": v(44.45, 0) * mm, "end": v(44.45, -12.7) * mm});
            skLineSegment(sketch, "E126", {"start": v(152.4, 0) * mm, "end": v(152.4, 25.4) * mm});
            skLineSegment(sketch, "E127.MirrorCS", {"start": v(292.1, -12.7) * mm, "end": v(260.35, -12.7) * mm});
            skLineSegment(sketch, "E128.MirrorCS", {"start": v(260.35, 0) * mm, "end": v(260.35, -12.7) * mm});
            skLineSegment(sketch, "E129.MirrorCS", {"start": v(292.1, 0) * mm, "end": v(260.35, 0) * mm});
            skLineSegment(sketch, "E130.MirrorCS", {"start": v(292.1, 0) * mm, "end": v(292.1, -12.7) * mm});
            skSolve(sketch);
        }
        {
            var Q0;
            Q0 = qSketchRegion(id + "F39", true);
            extrude(context, id + "F40", {"entities" : qUnion([Q0]), "oppositeDirection" : true, "depth" : 304.8 * mm});
        }
        {
            var Q0;
            Q0=makeQuery(id+"F40.opExtrude","SWEPT_FACE",FACE,{"disambiguationData":[OSD([sQuery(id+"F39.wireOp",EDGE,"E130.MirrorCS")])]});
            var sketch = newSketch(context, id + "F41", { "sketchPlane" : qUnion([Q0])});
            skLineSegment(sketch, "E131.bottom", {"start": v(279.4, -22.22) * mm, "end": v(266.7, -22.22) * mm});
            skLineSegment(sketch, "E131.top", {"start": v(279.4, 9.53) * mm, "end": v(266.7, 9.53) * mm});
            skLineSegment(sketch, "E131.left", {"start": v(279.4, -22.22) * mm, "end": v(279.4, 9.53) * mm});
            skLineSegment(sketch, "E131.right", {"start": v(266.7, -22.22) * mm, "end": v(266.7, 9.53) * mm});
            skPoint(sketch, "E132", {"position": v(266.7, -6.35) * mm});
            skSolve(sketch);
        }
        {
            var Q0;
            {var subQ3=sQuery(id+"F41.wireOp",EDGE,"E131.bottom");Q0=makeQuery(id+"F41.imprint","IMPRINT",FACE,{"disambiguationData":[TD([[makeQuery(id+"F41.imprint","IMPRINT",EDGE,{"derivedFrom":subQ3}),-1.0]])]});}
            extrude(context, id + "F42", {"entities" : qUnion([Q0]), "oppositeDirection" : true, "depth" : 279.4 * mm});
        }
        {
            var Q0;
            Q0=makeQuery(id+"F42.opExtrude","SWEPT_FACE",FACE,{"disambiguationData":[OSD([sQuery(id+"F41.wireOp",EDGE,"E131.bottom")])]});
            var sketch = newSketch(context, id + "F43", { "sketchPlane" : qUnion([Q0])});
            skLineSegment(sketch, "E133", {"start": v(279.4, 152.4) * mm, "end": v(266.7, 152.4) * mm});
            skLineSegment(sketch, "E134", {"start": v(266.7, 152.4) * mm, "end": v(209.27, 152.4) * mm});
            skLineSegment(sketch, "E135", {"start": v(266.7, 179.39) * mm, "end": v(234.95, 179.39) * mm});
            skLineSegment(sketch, "E136", {"start": v(234.95, 179.39) * mm, "end": v(234.95, 192.09) * mm});
            skLineSegment(sketch, "E137", {"start": v(234.95, 192.09) * mm, "end": v(241.3, 192.09) * mm});
            skLineSegment(sketch, "E138", {"start": v(241.3, 192.09) * mm, "end": v(241.3, 188.91) * mm});
            skLineSegment(sketch, "E139", {"start": v(241.3, 188.91) * mm, "end": v(266.7, 188.91) * mm});
            skLineSegment(sketch, "E140", {"start": v(266.7, 188.91) * mm, "end": v(266.7, 179.39) * mm});
            skPoint(sketch, "E141", {"position": v(266.7, 184.15) * mm});
            skLineSegment(sketch, "E142.MirrorCS", {"start": v(266.7, 125.41) * mm, "end": v(234.95, 125.41) * mm});
            skLineSegment(sketch, "E143.MirrorCS", {"start": v(266.7, 115.89) * mm, "end": v(266.7, 125.41) * mm});
            skLineSegment(sketch, "E144.MirrorCS", {"start": v(241.3, 115.89) * mm, "end": v(266.7, 115.89) * mm});
            skLineSegment(sketch, "E145.MirrorCS", {"start": v(241.3, 112.71) * mm, "end": v(241.3, 115.89) * mm});
            skLineSegment(sketch, "E146.MirrorCS", {"start": v(234.95, 112.71) * mm, "end": v(241.3, 112.71) * mm});
            skLineSegment(sketch, "E147.MirrorCS", {"start": v(234.95, 125.41) * mm, "end": v(234.95, 112.71) * mm});
            skSolve(sketch);
        }
        {
            var Q0;
            Q0=makeQuery(id+"F43.imprint","IMPRINT",FACE,{"disambiguationData":[TD([[makeQuery(id+"F43.imprint","IMPRINT",EDGE,{"derivedFrom":sQuery(id+"F43.wireOp",EDGE,"E142.MirrorCS")}),1.0]])]});
            var Q1;
            Q1=makeQuery(id+"F43.imprint","IMPRINT",FACE,{"disambiguationData":[TD([[makeQuery(id+"F43.imprint","IMPRINT",EDGE,{"derivedFrom":sQuery(id+"F43.wireOp",EDGE,"E135")}),-1.0]])]});
            extrude(context, id + "F44", {"entities" : qUnion([Q0, Q1]), "oppositeDirection" : true, "depth" : 304.8 * mm});
        }
        {
            var Q0;
            Q0=makeQuery(id+"F29.opExtrude","CAP_FACE",FACE,{"disambiguationData":[OSD([sQuery(id+"F28.wireOp",EDGE,"E70.bottom"),sQuery(id+"F28.wireOp",EDGE,"E70.top"),sQuery(id+"F28.wireOp",EDGE,"E70.left"),sQuery(id+"F28.wireOp",EDGE,"E70.right"),sQuery(id+"F28.wireOp",EDGE,"E73")])],"isStart":false});
            var sketch = newSketch(context, id + "F45", { "sketchPlane" : qUnion([Q0])});
            skLineSegment(sketch, "E148.bottom", {"start": v(-23.5, 8.25) * mm, "end": v(23.5, 8.25) * mm});
            skLineSegment(sketch, "E148.top", {"start": v(-23.5, 55.25) * mm, "end": v(23.5, 55.25) * mm});
            skLineSegment(sketch, "E148.left", {"start": v(-23.5, 8.25) * mm, "end": v(-23.5, 55.25) * mm});
            skLineSegment(sketch, "E148.right", {"start": v(23.5, 8.25) * mm, "end": v(23.5, 55.25) * mm});
            skPoint(sketch, "E149", {"position": v(0, 55.25) * mm});
            skPoint(sketch, "E150", {"position": v(23.5, 31.75) * mm});
            skPoint(sketch, "E151", {"position": v(0, 31.75) * mm});
            skLineSegment(sketch, "E152.bottom", {"start": v(-28.5, 3.25) * mm, "end": v(28.5, 3.25) * mm});
            skLineSegment(sketch, "E152.top", {"start": v(-28.5, 60.25) * mm, "end": v(28.5, 60.25) * mm});
            skLineSegment(sketch, "E152.left", {"start": v(-28.5, 3.25) * mm, "end": v(-28.5, 60.25) * mm});
            skLineSegment(sketch, "E152.right", {"start": v(28.5, 3.25) * mm, "end": v(28.5, 60.25) * mm});
            skLineSegment(sketch, "E153", {"start": v(-28.5, 3.25) * mm, "end": v(28.5, 60.25) * mm});
            skCircle(sketch, "E154", {"center": v(-23.5, 55.25) * mm, "radius": 2.5 * mm});
            skCircle(sketch, "E155", {"center": v(23.5, 55.25) * mm, "radius": 2.5 * mm});
            skCircle(sketch, "E156", {"center": v(23.5, 8.25) * mm, "radius": 2.5 * mm});
            skCircle(sketch, "E157", {"center": v(-23.5, 8.25) * mm, "radius": 2.5 * mm});
            skLineSegment(sketch, "E158.top", {"start": v(-28.5, -5.64) * mm, "end": v(28.5, -5.64) * mm});
            skLineSegment(sketch, "E158.left", {"start": v(-28.5, 3.25) * mm, "end": v(-28.5, -5.64) * mm});
            skLineSegment(sketch, "E158.right", {"start": v(28.5, 3.25) * mm, "end": v(28.5, -5.64) * mm});
            skLineSegment(sketch, "E159", {"start": v(-28.5, -1.2) * mm, "end": v(28.5, -1.2) * mm});
            skLineSegment(sketch, "E160", {"start": v(0, 55.25) * mm, "end": v(0, -5.64) * mm});
            skCircle(sketch, "E161", {"center": v(-12.7, -1.2) * mm, "radius": 3.18 * mm});
            skCircle(sketch, "E162.MirrorC", {"center": v(12.7, -1.2) * mm, "radius": 3.18 * mm});
            skSolve(sketch);
        }
        {
            var Q0;
            Q0 = qSketchRegion(id + "F45", true);
            var Q1;
            {var subQ6=sQuery(id+"F45.wireOp",EDGE,"E157");var subQ12=sQuery(id+"F45.wireOp",EDGE,"E148.bottom");var subQ14=makeQuery(id+"F45.imprint","INTERSECT",VERTEX,{"derivedFrom":[subQ12,subQ6]});Q1=makeQuery(id+"F45.imprint","IMPRINT",FACE,{"disambiguationData":[TD([[makeQuery(id+"F45.imprint","IMPRINT",EDGE,{"disambiguationData":[TD([[subQ14,-1.0]])],"derivedFrom":subQ12}),1.0]])]});}
            var Q2;
            {var subQ5=sQuery(id+"F45.wireOp",EDGE,"E157");var subQ6=sQuery(id+"F45.wireOp",EDGE,"E148.left");var subQ7=makeQuery(id+"F45.imprint","INTERSECT",VERTEX,{"derivedFrom":[subQ6,subQ5]});Q2=makeQuery(id+"F45.imprint","IMPRINT",FACE,{"disambiguationData":[TD([[makeQuery(id+"F45.imprint","IMPRINT",EDGE,{"disambiguationData":[TD([[subQ7,-1.0]])],"derivedFrom":subQ6}),-1.0]])]});}
            var Q3;
            {var subQ5=sQuery(id+"F45.wireOp",EDGE,"E154");var subQ9=sQuery(id+"F45.wireOp",EDGE,"E148.top");var subQ10=makeQuery(id+"F45.imprint","INTERSECT",VERTEX,{"derivedFrom":[subQ9,subQ5]});Q3=makeQuery(id+"F45.imprint","IMPRINT",FACE,{"disambiguationData":[TD([[makeQuery(id+"F45.imprint","IMPRINT",EDGE,{"disambiguationData":[TD([[subQ10,-1.0]])],"derivedFrom":subQ9}),-1.0]])]});}
            var Q4;
            {var subQ0=sQuery(id+"F45.wireOp",EDGE,"E155");var subQ1=sQuery(id+"F45.wireOp",EDGE,"E148.right");var subQ2=makeQuery(id+"F45.imprint","INTERSECT",VERTEX,{"derivedFrom":[subQ1,subQ0]});Q4=makeQuery(id+"F45.imprint","IMPRINT",FACE,{"disambiguationData":[TD([[makeQuery(id+"F45.imprint","IMPRINT",EDGE,{"disambiguationData":[TD([[subQ2,1.0]])],"derivedFrom":subQ1}),1.0]])]});}
            var Q5;
            {var subQ5=sQuery(id+"F45.wireOp",EDGE,"E160");var subQ6=sQuery(id+"F45.wireOp",EDGE,"E148.bottom");var subQ7=makeQuery(id+"F45.imprint","INTERSECT",VERTEX,{"derivedFrom":[subQ6,subQ5]});Q5=makeQuery(id+"F45.imprint","IMPRINT",FACE,{"disambiguationData":[TD([[makeQuery(id+"F45.imprint","IMPRINT",EDGE,{"disambiguationData":[TD([[subQ7,-1.0]])],"derivedFrom":subQ6}),1.0]])]});}
            var Q6;
            {var subQ1=sQuery(id+"F45.wireOp",EDGE,"E148.top");var subQ7=sQuery(id+"F45.wireOp",EDGE,"E160");var subQ8=makeQuery(id+"F45.imprint","INTERSECT",VERTEX,{"derivedFrom":[subQ1,subQ7]});Q6=makeQuery(id+"F45.imprint","IMPRINT",FACE,{"disambiguationData":[TD([[makeQuery(id+"F45.imprint","IMPRINT",EDGE,{"disambiguationData":[TD([[subQ8,-1.0]])],"derivedFrom":subQ1}),-1.0]])]});}
            var Q7;
            {var subQ0=sQuery(id+"F45.wireOp",EDGE,"E153");var subQ1=makeQuery(id+"F29.opExtrude","CAP_EDGE",EDGE,{"disambiguationData":[OSD([sQuery(id+"F28.wireOp",EDGE,"E73")])],"isStart":false});var subQ2=makeQuery(id+"F45.imprint","INTERSECT",VERTEX,{"disambiguationData":[OD(1.0)],"derivedFrom":[subQ1,subQ0]});Q7=makeQuery(id+"F45.imprint","IMPRINT",FACE,{"disambiguationData":[TD([[makeQuery(id+"F45.imprint","IMPRINT",EDGE,{"disambiguationData":[TD([[subQ2,-1.0]])],"derivedFrom":subQ0}),1.0]])]});}
            extrude(context, id + "F46", {"entities" : qUnion([Q0, Q1, Q2, Q3, Q4, Q5, Q6, Q7]), "depth" : 38.1 * mm, "hasSecondDirection" : true, "secondDirectionOppositeDirection" : false, "secondDirectionDepth" : 28.57 * mm});
        }
        {
            var Q0;
            Q0=makeQuery(id+"F46.opExtrude","CAP_FACE",FACE,{"disambiguationData":[OSD([sQuery(id+"F28.wireOp",EDGE,"E73"),sQuery(id+"F45.wireOp",EDGE,"E152.top"),sQuery(id+"F45.wireOp",EDGE,"E152.left"),sQuery(id+"F45.wireOp",EDGE,"E152.right"),sQuery(id+"F45.wireOp",EDGE,"E154"),sQuery(id+"F45.wireOp",EDGE,"E155"),sQuery(id+"F45.wireOp",EDGE,"E156"),sQuery(id+"F45.wireOp",EDGE,"E157"),sQuery(id+"F45.wireOp",EDGE,"E158.top"),sQuery(id+"F45.wireOp",EDGE,"E158.left"),sQuery(id+"F45.wireOp",EDGE,"E158.right"),sQuery(id+"F45.wireOp",EDGE,"uYML9c6I-88PV-zpJg-Jb4t-KMMiFPHjWHLG"),sQuery(id+"F45.wireOp",EDGE,"E161"),sQuery(id+"F45.wireOp",EDGE,"E162.MirrorC")])],"isStart":false});
            var sketch = newSketch(context, id + "F47", { "sketchPlane" : qUnion([Q0])});
            skCircle(sketch, "E163", {"center": v(-12.7, -1.2) * mm, "radius": 5.72 * mm});
            skCircle(sketch, "E164", {"center": v(12.7, -1.2) * mm, "radius": 5.72 * mm});
            skSolve(sketch);
        }
        {
            var Q0;
            Q0 = qSketchRegion(id + "F47", true);
            extrude(context, id + "F48", {"entities" : qUnion([Q0]), "operationType" : NewBodyOperationType.REMOVE, "oppositeDirection" : true, "depth" : 3.17 * mm});
        }
        {
            var Q0;
            Q0=makeQuery(id+"F44.opExtrude","SWEPT_FACE",FACE,{"disambiguationData":[OSD([sQuery(id+"F43.wireOp",EDGE,"E144.MirrorCS")])]});
            var sketch = newSketch(context, id + "F49", { "sketchPlane" : qUnion([Q0])});
            skLineSegment(sketch, "E165.bottom", {"start": v(-266.7, 269.88) * mm, "end": v(-279.4, 269.88) * mm});
            skLineSegment(sketch, "E165.top", {"start": v(-266.7, 238.13) * mm, "end": v(-279.4, 238.13) * mm});
            skLineSegment(sketch, "E165.left", {"start": v(-266.7, 269.88) * mm, "end": v(-266.7, 238.13) * mm});
            skLineSegment(sketch, "E165.right", {"start": v(-279.4, 269.88) * mm, "end": v(-279.4, 238.13) * mm});
            skSolve(sketch);
        }
        {
            var Q0;
            Q0 = qSketchRegion(id + "F49", true);
            extrude(context, id + "F50", {"entities" : qUnion([Q0]), "oppositeDirection" : true, "depth" : 76.2 * mm - 3.17 * mm});
        }
        {
            var Q0;
            Q0=qCreatedBy(makeId("Front.planeOp"),FACE);
            var sketch = newSketch(context, id + "F51", { "sketchPlane" : qUnion([Q0])});
            skLineSegment(sketch, "E166.bottom", {"start": v(-52.34, 185.59) * mm, "end": v(55.64, 185.59) * mm});
            skLineSegment(sketch, "E166.top", {"start": v(-52.34, 88.7) * mm, "end": v(55.64, 88.7) * mm});
            skLineSegment(sketch, "E166.left", {"start": v(-52.34, 185.59) * mm, "end": v(-52.34, 88.7) * mm});
            skLineSegment(sketch, "E166.right", {"start": v(55.64, 185.59) * mm, "end": v(55.64, 88.7) * mm});
            skSolve(sketch);
        }
        {
            var Q0;
            Q0=makeQuery(id+"F51.imprint","IMPRINT",FACE,{"disambiguationData":[TD([[makeQuery(id+"F51.imprint","IMPRINT",EDGE,{"derivedFrom":sQuery(id+"F51.wireOp",EDGE,"E166.bottom")}),-1.0]])]});
            var Q1;
            Q1=sQuery(id+"F51.wireOp",EDGE,"E166.right");
            extrude(context, id + "F52", {"entities" : qUnion([Q0]), "surfaceEntities" : qUnion([Q1]), "depth" : 101.6 * mm});
        }
        {
            var Q0;
            Q0=makeQuery(id+"F52.opExtrude","SWEPT_FACE",FACE,{"disambiguationData":[OSD([sQuery(id+"F51.wireOp",EDGE,"E166.right")])]});
            var sketch = newSketch(context, id + "F53", { "sketchPlane" : qUnion([Q0])});
            skCircle(sketch, "E167", {"center": v(-45.4, 151.72) * mm, "radius": 19.08 * mm});
            skSolve(sketch);
        }
        {
            var Q0;
            Q0 = qSketchRegion(id + "F53", true);
            extrude(context, id + "F54", {"entities" : qUnion([Q0]), "operationType" : NewBodyOperationType.ADD, "depth" : 25.4 * mm});
        }
    });
